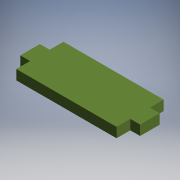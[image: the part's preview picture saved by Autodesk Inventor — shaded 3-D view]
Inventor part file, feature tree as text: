
AUTODESK INVENTOR PART (.ipt)
format: ipt  version: 2017 (Build 210142000, 142)  size: 92,672 bytes
history: native  units: mm (DEFAULTED — no unit token found)
features: extrude x1
ambient origin geometry x8: Origin, YZ Plane, XZ Plane, XY Plane, X Axis, Y Axis, Z Axis, Center Point
bodies: Solid1 (feature_tree)
feature tree (1):
  extrude  "Extrusion1"  Depth=24.0mm
